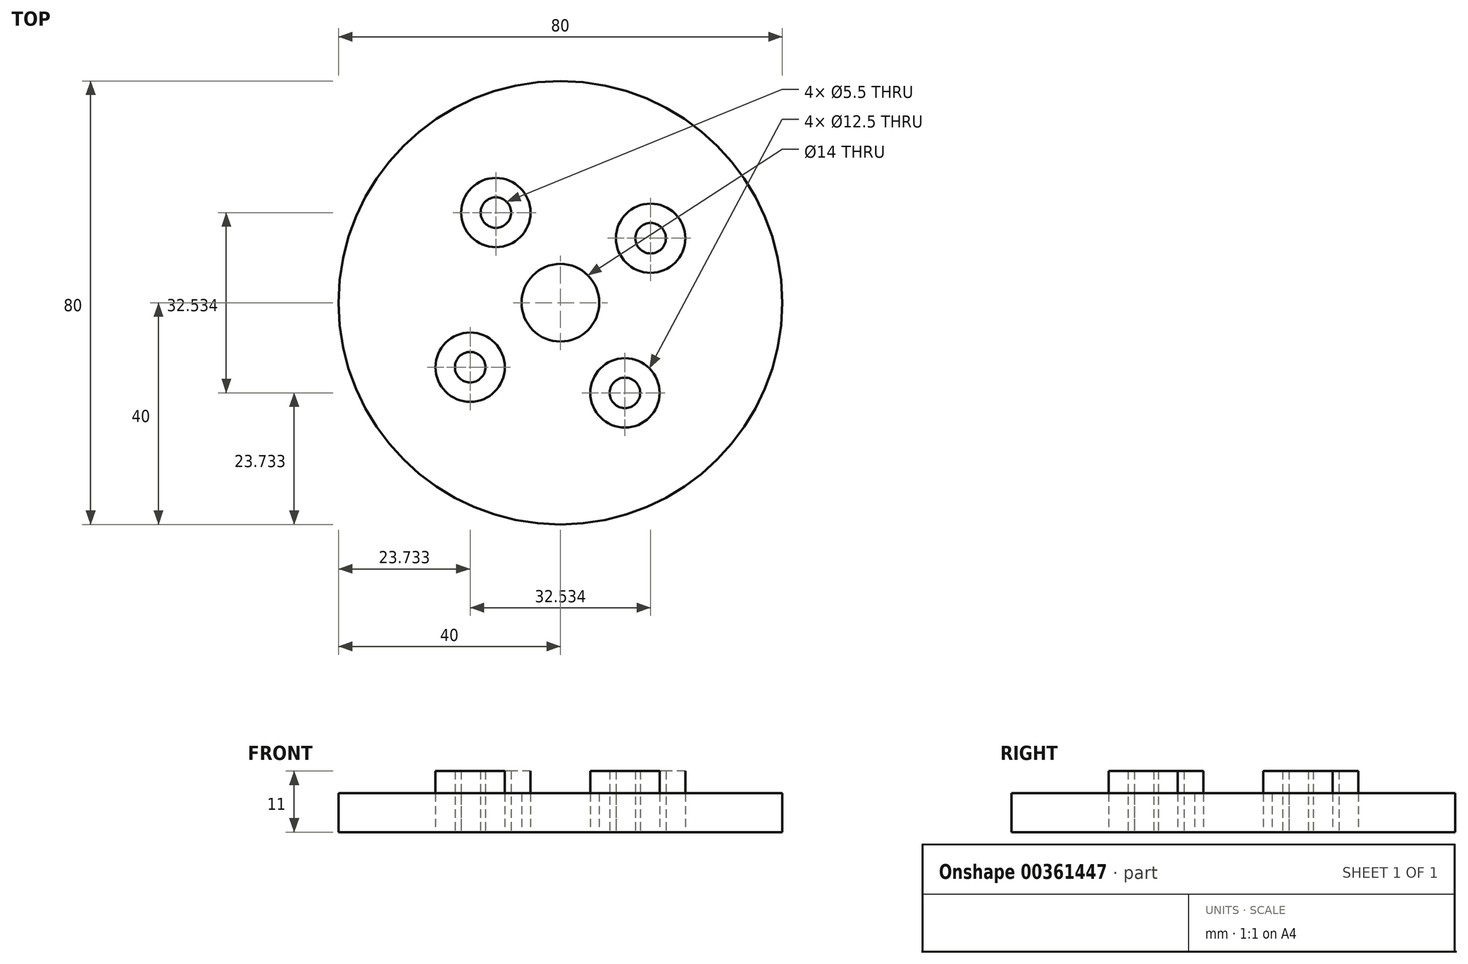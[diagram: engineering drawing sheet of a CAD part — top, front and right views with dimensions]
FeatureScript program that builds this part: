
annotation { "Feature Type Name" : "Feature", "Feature Type Description" : "" }
export const myFeature = defineFeature(function(context is Context, id is Id, definition is map)
    precondition{}
    {
        {
            var Q0;
            Q0=qCreatedBy(makeId("Top.planeOp"),FACE);
            var sketch = newSketch(context, id + "F0", { "sketchPlane" : qUnion([Q0])});
            skCircle(sketch, "E0", {"center": v(0, 0) * mm, "radius": 40 * mm});
            skLineSegment(sketch, "E1", {"start": v(0, 0) * mm, "end": v(32.53, 23.27) * mm, "construction": true});
            skLineSegment(sketch, "E2", {"start": v(16.27, 11.64) * mm, "end": v(0, 0) * mm, "construction": true});
            skCircle(sketch, "E3", {"center": v(16.27, 11.64) * mm, "radius": 2.75 * mm});
            skLineSegment(sketch, "E4", {"start": v(32.53, 23.27) * mm, "end": v(-32.53, -23.27) * mm, "construction": true});
            skLineSegment(sketch, "E5", {"start": v(-32.53, -23.27) * mm, "end": v(-16.27, -11.64) * mm, "construction": true});
            skCircle(sketch, "E6", {"center": v(-16.27, -11.64) * mm, "radius": 2.75 * mm});
            skLineSegment(sketch, "E7", {"start": v(0, 0) * mm, "end": v(23.27, -32.53) * mm, "construction": true});
            skLineSegment(sketch, "E8", {"start": v(23.27, -32.53) * mm, "end": v(-23.27, 32.53) * mm, "construction": true});
            skLineSegment(sketch, "E9", {"start": v(-23.27, 32.53) * mm, "end": v(-11.64, 16.27) * mm, "construction": true});
            skLineSegment(sketch, "E10", {"start": v(11.64, -16.27) * mm, "end": v(0, 0) * mm, "construction": true});
            skCircle(sketch, "E11", {"center": v(-11.64, 16.27) * mm, "radius": 2.75 * mm});
            skCircle(sketch, "E12", {"center": v(11.64, -16.27) * mm, "radius": 2.75 * mm});
            skCircle(sketch, "E13", {"center": v(0, 0) * mm, "radius": 3.4 * mm});
            skCircle(sketch, "E14", {"center": v(0, 0) * mm, "radius": 7 * mm});
            skCircle(sketch, "E15", {"center": v(-11.64, 16.27) * mm, "radius": 6.25 * mm});
            skCircle(sketch, "E16", {"center": v(-16.27, -11.64) * mm, "radius": 6.25 * mm});
            skCircle(sketch, "E17", {"center": v(16.27, 11.64) * mm, "radius": 6.25 * mm});
            skCircle(sketch, "E18", {"center": v(11.64, -16.27) * mm, "radius": 6.25 * mm});
            skSolve(sketch);
        }
        {
            var Q0;
            Q0 = qSketchRegion(id + "F0", true);
            extrude(context, id + "F1", {"entities" : qUnion([Q0]), "depth" : 7 * mm});
        }
        {
            var Q0;
            Q0=makeQuery(id+"F0.imprint","IMPRINT",FACE,{"disambiguationData":[TD([[makeQuery(id+"F0.imprint","IMPRINT",EDGE,{"derivedFrom":sQuery(id+"F0.wireOp",EDGE,"E11")}),-1.0]])]});
            var Q1;
            Q1=makeQuery(id+"F0.imprint","IMPRINT",FACE,{"disambiguationData":[TD([[makeQuery(id+"F0.imprint","IMPRINT",EDGE,{"derivedFrom":sQuery(id+"F0.wireOp",EDGE,"E6")}),-1.0]])]});
            var Q2;
            Q2=makeQuery(id+"F0.imprint","IMPRINT",FACE,{"disambiguationData":[TD([[makeQuery(id+"F0.imprint","IMPRINT",EDGE,{"derivedFrom":sQuery(id+"F0.wireOp",EDGE,"E12")}),-1.0]])]});
            var Q3;
            Q3=makeQuery(id+"F0.imprint","IMPRINT",FACE,{"disambiguationData":[TD([[makeQuery(id+"F0.imprint","IMPRINT",EDGE,{"derivedFrom":sQuery(id+"F0.wireOp",EDGE,"E3")}),-1.0]])]});
            extrude(context, id + "F2", {"entities" : qUnion([Q0, Q1, Q2, Q3]), "depth" : 11 * mm});
        }
    });
